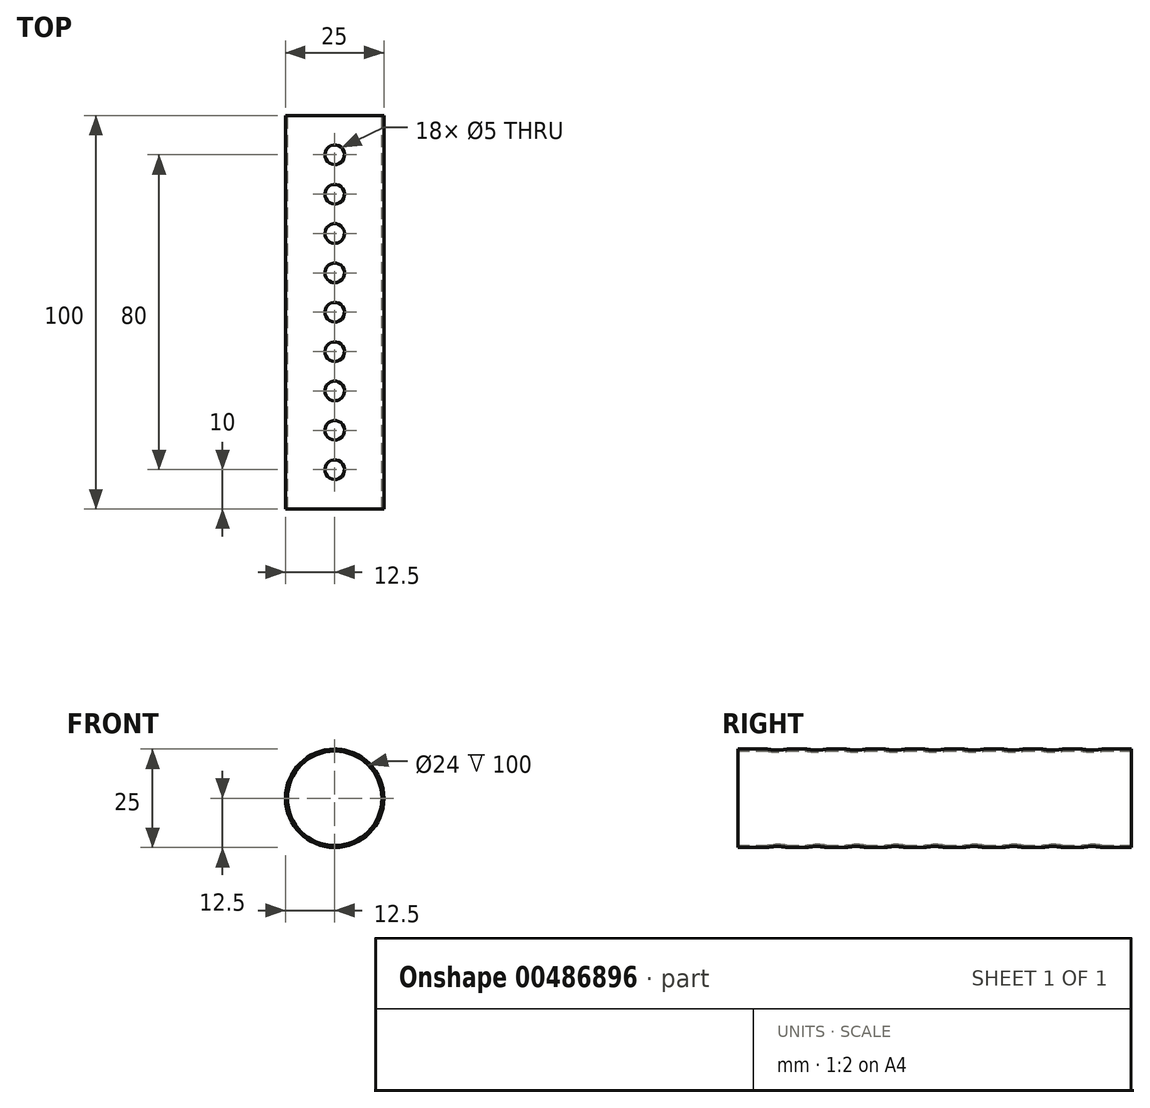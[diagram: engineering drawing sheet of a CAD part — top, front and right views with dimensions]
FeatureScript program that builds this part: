
annotation { "Feature Type Name" : "Feature", "Feature Type Description" : "" }
export const myFeature = defineFeature(function(context is Context, id is Id, definition is map)
    precondition{}
    {
        {
            var Q0;
            Q0=qCreatedBy(makeId("Front.planeOp"),FACE);
            var sketch = newSketch(context, id + "F0", { "sketchPlane" : qUnion([Q0])});
            skCircle(sketch, "E0", {"center": v(0, 0) * mm, "radius": 12.5 * mm});
            skCircle(sketch, "E1", {"center": v(0, 0) * mm, "radius": 12 * mm});
            skSolve(sketch);
        }
        {
            var Q0;
            Q0 = qSketchRegion(id + "F0", true);
            extrude(context, id + "F1", {"entities" : qUnion([Q0]), "depth" : 100 * mm});
        }
        {
            var Q0;
            Q0=qCreatedBy(makeId("Top.planeOp"),FACE);
            var sketch = newSketch(context, id + "F2", { "sketchPlane" : qUnion([Q0])});
            skCircle(sketch, "E2", {"center": v(0, -10) * mm, "radius": 2.5 * mm});
            skCircle(sketch, "E3", {"center": v(0, -20) * mm, "radius": 2.5 * mm});
            skCircle(sketch, "E4", {"center": v(0, -30) * mm, "radius": 2.5 * mm});
            skCircle(sketch, "E5", {"center": v(0, -40) * mm, "radius": 2.5 * mm});
            skCircle(sketch, "E6", {"center": v(0, -50) * mm, "radius": 2.5 * mm});
            skCircle(sketch, "E7", {"center": v(0, -60) * mm, "radius": 2.5 * mm});
            skCircle(sketch, "E8", {"center": v(0, -70) * mm, "radius": 2.5 * mm});
            skCircle(sketch, "E9", {"center": v(0, -90) * mm, "radius": 2.5 * mm});
            skCircle(sketch, "E10", {"center": v(0, -80) * mm, "radius": 2.5 * mm});
            skCircle(sketch, "E11", {"center": v(0, -107.06) * mm, "radius": 2.12 * mm});
            skSolve(sketch);
        }
        {
            var Q0;
            Q0 = qSketchRegion(id + "F2", true);
            extrude(context, id + "F3", {"entities" : qUnion([Q0]), "operationType" : NewBodyOperationType.REMOVE, "endBound" : BoundingType.SYMMETRIC, "depth" : 25 * mm});
        }
    });
